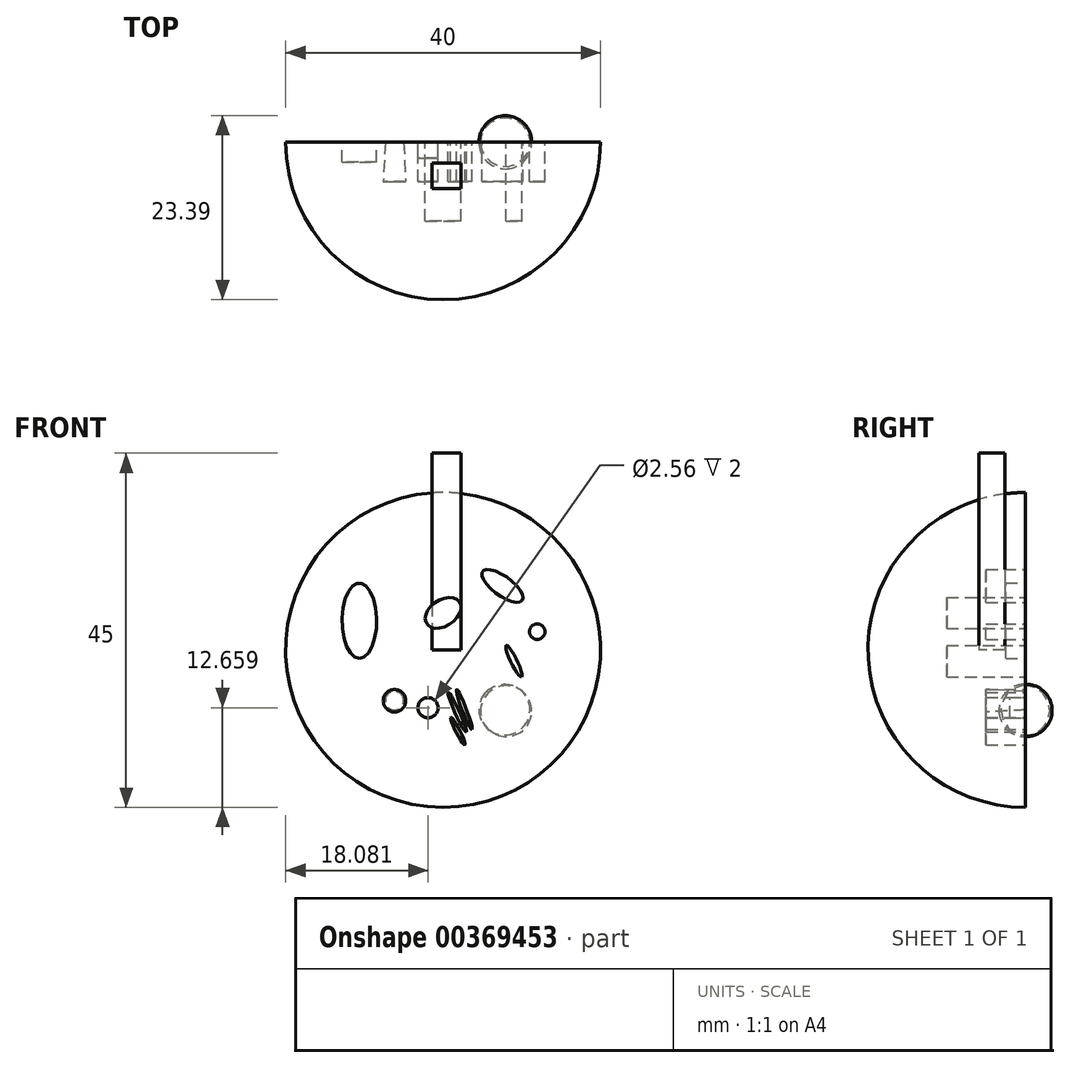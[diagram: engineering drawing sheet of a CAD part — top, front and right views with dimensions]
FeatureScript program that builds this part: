
annotation { "Feature Type Name" : "Feature", "Feature Type Description" : "" }
export const myFeature = defineFeature(function(context is Context, id is Id, definition is map)
    precondition{}
    {
        {
            var Q0;
            Q0=qCreatedBy(makeId("Front.planeOp"),FACE);
            var sketch = newSketch(context, id + "F0", { "sketchPlane" : qUnion([Q0])});
            skCircle(sketch, "E0", {"center": v(0, 0) * mm, "radius": 20 * mm});
            skLineSegment(sketch, "E1", {"start": v(0, 20) * mm, "end": v(0, -20) * mm});
            skSolve(sketch);
        }
        {
            var Q0;
            {var subQ0=sQuery(id+"F0.wireOp",EDGE,"E1");Q0=makeQuery(id+"F0.imprint","IMPRINT",FACE,{"disambiguationData":[TD([[makeQuery(id+"F0.imprint","IMPRINT",EDGE,{"derivedFrom":subQ0}),1.0]])]});}
            var Q1;
            Q1=sQuery(id+"F0.wireOp",EDGE,"E1");
            revolve(context, id + "F1", {"entities" : qUnion([Q0]), "axis" : qUnion([Q1]), "revolveType" : RevolveType.ONE_DIRECTION, "angle" : 180 * degree});
        }
        {
            var Q0;
            Q0=qCreatedBy(makeId("Front.planeOp"),FACE);
            var sketch = newSketch(context, id + "F2", { "sketchPlane" : qUnion([Q0])});
            skCircle(sketch, "E2", {"center": v(0, 0) * mm, "radius": 16.97 * mm});
            skSolve(sketch);
        }
        {
            var Q0;
            Q0=makeQuery(id+"F2.imprint","IMPRINT",FACE,{"disambiguationData":[TD([[makeQuery(id+"F2.imprint","IMPRINT",EDGE,{"derivedFrom":sQuery(id+"F2.wireOp",EDGE,"E2")}),1.0]])]});
            extrude(context, id + "F3", {"entities" : qUnion([Q0]), "operationType" : NewBodyOperationType.REMOVE, "depth" : 2 * mm});
        }
        {
            var Q0;
            Q0=makeQuery(id+"F2.imprint","IMPRINT",FACE,{"disambiguationData":[TD([[makeQuery(id+"F2.imprint","IMPRINT",EDGE,{"derivedFrom":sQuery(id+"F2.wireOp",EDGE,"E2")}),1.0]])]});
            var sketch = newSketch(context, id + "F4", { "sketchPlane" : qUnion([Q0])});
            skLineSegment(sketch, "E3", {"start": v(10.1, -5.3) * mm, "end": v(5.71, -10.06) * mm});
            skArc(sketch, "E4", {"start": v(10.1, -5.3) * mm, "mid": v(5.41, -5.39) * mm, "end": v(5.71, -10.06) * mm});
            skSolve(sketch);
        }
        {
            var Q0;
            Q0 = qSketchRegion(id + "F4", true);
            var Q1;
            Q1=sQuery(id+"F4.wireOp",EDGE,"E3");
            revolve(context, id + "F5", {"entities" : qUnion([Q0]), "axis" : qUnion([Q1]), "revolveType" : RevolveType.FULL});
        }
        {
            var Q0;
            Q0=makeQuery(id+"F2.imprint","IMPRINT",FACE,{"disambiguationData":[TD([[makeQuery(id+"F2.imprint","IMPRINT",EDGE,{"derivedFrom":sQuery(id+"F2.wireOp",EDGE,"E2")}),1.0]])]});
            var sketch = newSketch(context, id + "F6", { "sketchPlane" : qUnion([Q0])});
            skEllipse(sketch, "E5", {"center": v(-10.64, 3.72) * mm, "majorRadius": 4.78 * mm, "minorRadius": 2.2 * mm, "majorAxis": v(0, -1)});
            skSolve(sketch);
        }
        {
            var Q0;
            Q0 = qSketchRegion(id + "F6", true);
            extrude(context, id + "F7", {"entities" : qUnion([Q0]), "depth" : 2.5 * mm});
        }
        {
            var Q0;
            Q0=makeQuery(id+"F4.imprint","IMPRINT",FACE,{"disambiguationData":[TD([[makeQuery(id+"F4.imprint","IMPRINT",EDGE,{"derivedFrom":sQuery(id+"F4.wireOp",EDGE,"E3")}),1.0]])]});
            var sketch = newSketch(context, id + "F8", { "sketchPlane" : qUnion([Q0])});
            skEllipse(sketch, "E6", {"center": v(7.53, 8.13) * mm, "majorRadius": 3.12 * mm, "minorRadius": 1.24 * mm, "majorAxis": v(0.8, -0.6)});
            skSolve(sketch);
        }
        {
            var Q0;
            Q0=makeQuery(id+"F8.imprint","IMPRINT",FACE,{"disambiguationData":[TD([[makeQuery(id+"F8.imprint","IMPRINT",EDGE,{"derivedFrom":sQuery(id+"F8.wireOp",EDGE,"E6")}),1.0]])]});
            var sketch = newSketch(context, id + "F9", { "sketchPlane" : qUnion([Q0])});
            skSolve(sketch);
        }
        {
            var Q0;
            Q0 = qSketchRegion(id + "F8", true);
            extrude(context, id + "F10", {"entities" : qUnion([Q0]), "depth" : 5 * mm});
        }
        {
            var Q0;
            Q0=makeQuery(id+"F4.imprint","IMPRINT",FACE,{"disambiguationData":[TD([[makeQuery(id+"F4.imprint","IMPRINT",EDGE,{"derivedFrom":sQuery(id+"F4.wireOp",EDGE,"E3")}),1.0]])]});
            var sketch = newSketch(context, id + "F11", { "sketchPlane" : qUnion([Q0])});
            skCircle(sketch, "E7", {"center": v(-6.17, -6.45) * mm, "radius": 1.17 * mm});
            skPoint(sketch, "E7.first.point", {"position": v(-7.1, -7.15) * mm});
            skPoint(sketch, "E7.second.point", {"position": v(-5.1, -6) * mm});
            skPoint(sketch, "E7.third.point", {"position": v(-6.5, -5.34) * mm});
            skSolve(sketch);
        }
        {
            var Q0;
            Q0 = qSketchRegion(id + "F11", true);
            extrude(context, id + "F12", {"entities" : qUnion([Q0]), "depth" : 5 * mm, "hasDraft" : true, "draftAngle" : 3 * degree});
        }
        {
            var Q0;
            Q0=makeQuery(id+"F2.imprint","IMPRINT",FACE,{"disambiguationData":[TD([[makeQuery(id+"F2.imprint","IMPRINT",EDGE,{"derivedFrom":sQuery(id+"F2.wireOp",EDGE,"E2")}),1.0]])]});
            var sketch = newSketch(context, id + "F13", { "sketchPlane" : qUnion([Q0])});
            skCircle(sketch, "E8", {"center": v(-1.92, -7.34) * mm, "radius": 1.28 * mm});
            skSolve(sketch);
        }
        {
            var Q0;
            Q0 = qSketchRegion(id + "F13", true);
            var sketch = newSketch(context, id + "F14", { "sketchPlane" : qUnion([Q0])});
            skCircle(sketch, "E9", {"center": v(11.96, 2.32) * mm, "radius": 0.99 * mm});
            skSolve(sketch);
        }
        {
            var Q0;
            Q0=makeQuery(id+"F13.imprint","IMPRINT",FACE,{"disambiguationData":[TD([[makeQuery(id+"F13.imprint","IMPRINT",EDGE,{"derivedFrom":sQuery(id+"F13.wireOp",EDGE,"E8")}),-1.0]])]});
            var sketch = newSketch(context, id + "F15", { "sketchPlane" : qUnion([Q0])});
            skEllipse(sketch, "E10", {"center": v(0, 4.7) * mm, "majorRadius": 2.5 * mm, "minorRadius": 1.67 * mm, "majorAxis": v(0.83, 0.55)});
            skSolve(sketch);
        }
        {
            var Q0;
            Q0 = qSketchRegion(id + "F15", true);
            extrude(context, id + "F16", {"entities" : qUnion([Q0]), "depth" : 10 * mm});
        }
        {
            var Q0;
            Q0 = qSketchRegion(id + "F14", true);
            var Q1;
            Q1 = qSketchRegion(id + "F13", true);
            extrude(context, id + "F17", {"entities" : qUnion([Q0, Q1]), "depth" : 5 * mm});
        }
        {
            var Q0;
            Q0=makeQuery(id+"F13.imprint","IMPRINT",FACE,{"disambiguationData":[TD([[makeQuery(id+"F13.imprint","IMPRINT",EDGE,{"derivedFrom":sQuery(id+"F13.wireOp",EDGE,"E8")}),-1.0]])]});
            extrude(context, id + "F18", {"entities" : qUnion([Q0]), "depth" : 5 * mm});
        }
        {
            var Q0;
            Q0=makeQuery(id+"F15.imprint","IMPRINT",FACE,{"disambiguationData":[TD([[makeQuery(id+"F15.imprint","IMPRINT",EDGE,{"derivedFrom":sQuery(id+"F15.wireOp",EDGE,"E10")}),-1.0]])]});
            var sketch = newSketch(context, id + "F19", { "sketchPlane" : qUnion([Q0])});
            skEllipse(sketch, "E11", {"center": v(8.99, -1.41) * mm, "majorRadius": 2.22 * mm, "minorRadius": 0.4 * mm, "majorAxis": v(0.43, -0.9)});
            skSolve(sketch);
        }
        {
            var Q0;
            Q0 = qSketchRegion(id + "F19", true);
            extrude(context, id + "F20", {"entities" : qUnion([Q0]), "depth" : 10 * mm});
        }
        {
            var Q0;
            Q0=makeQuery(id+"F19.imprint","IMPRINT",FACE,{"disambiguationData":[TD([[makeQuery(id+"F19.imprint","IMPRINT",EDGE,{"derivedFrom":sQuery(id+"F19.wireOp",EDGE,"E11")}),-1.0]])]});
            var sketch = newSketch(context, id + "F21", { "sketchPlane" : qUnion([Q0])});
            skEllipse(sketch, "E12", {"center": v(1.8, -7.92) * mm, "majorRadius": 2.77 * mm, "minorRadius": 0.29 * mm, "majorAxis": v(0.41, -0.91)});
            skSolve(sketch);
        }
        {
            var Q0;
            Q0=makeQuery(id+"F19.imprint","IMPRINT",FACE,{"disambiguationData":[TD([[makeQuery(id+"F19.imprint","IMPRINT",EDGE,{"derivedFrom":sQuery(id+"F19.wireOp",EDGE,"E11")}),-1.0]])]});
            var sketch = newSketch(context, id + "F22", { "sketchPlane" : qUnion([Q0])});
            skEllipse(sketch, "E13", {"center": v(1.87, -10.31) * mm, "majorRadius": 1.96 * mm, "minorRadius": 0.26 * mm, "majorAxis": v(-0.45, 0.9)});
            skSolve(sketch);
        }
        {
            var Q0;
            Q0=makeQuery(id+"F19.imprint","IMPRINT",FACE,{"disambiguationData":[TD([[makeQuery(id+"F19.imprint","IMPRINT",EDGE,{"derivedFrom":sQuery(id+"F19.wireOp",EDGE,"E11")}),-1.0]])]});
            var sketch = newSketch(context, id + "F23", { "sketchPlane" : qUnion([Q0])});
            skEllipse(sketch, "E14", {"center": v(2.69, -7.55) * mm, "majorRadius": 2.7 * mm, "minorRadius": 0.28 * mm, "majorAxis": v(0.36, -0.93)});
            skSolve(sketch);
        }
        {
            var Q0;
            Q0 = qSketchRegion(id + "F22", true);
            extrude(context, id + "F24", {"entities" : qUnion([Q0]), "operationType" : NewBodyOperationType.ADD, "depth" : 10 * mm});
        }
        {
            var Q0;
            Q0 = qSketchRegion(id + "F23", true);
            extrude(context, id + "F25", {"entities" : qUnion([Q0]), "depth" : 5 * mm});
        }
        {
            var Q0;
            Q0 = qSketchRegion(id + "F21", true);
            extrude(context, id + "F26", {"entities" : qUnion([Q0]), "depth" : 5 * mm});
        }
        {
            var Q0;
            Q0 = qSketchRegion(id + "F22", true);
            extrude(context, id + "F27", {"entities" : qUnion([Q0]), "depth" : 5 * mm});
        }
        {
            var Q0;
            Q0=qCreatedBy(makeId("Top.planeOp"),FACE);
            var sketch = newSketch(context, id + "F28", { "sketchPlane" : qUnion([Q0])});
            skLineSegment(sketch, "E15.bottom", {"start": v(-1.38, -2.62) * mm, "end": v(2.25, -2.62) * mm});
            skLineSegment(sketch, "E15.top", {"start": v(-1.38, -5.9) * mm, "end": v(2.25, -5.9) * mm});
            skLineSegment(sketch, "E15.left", {"start": v(-1.38, -2.62) * mm, "end": v(-1.38, -5.9) * mm});
            skLineSegment(sketch, "E15.right", {"start": v(2.25, -2.62) * mm, "end": v(2.25, -5.9) * mm});
            skSolve(sketch);
        }
        {
            var Q0;
            Q0 = qSketchRegion(id + "F28", true);
            extrude(context, id + "F29", {"entities" : qUnion([Q0]), "depth" : 25 * mm});
        }
        {
            var Q0;
            Q0=qCreatedBy(makeId("Front.planeOp"),FACE);
            var sketch = newSketch(context, id + "F30", { "sketchPlane" : qUnion([Q0])});
            skCircle(sketch, "E16", {"center": v(0.42, 23.93) * mm, "radius": 1.11 * mm});
            skSolve(sketch);
        }
        {
            var Q0;
            Q0 = qSketchRegion(id + "F30", true);
            extrude(context, id + "F31", {"entities" : qUnion([Q0]), "operationType" : NewBodyOperationType.REMOVE, "oppositeDirection" : true, "depth" : 25 * mm});
        }
    });
